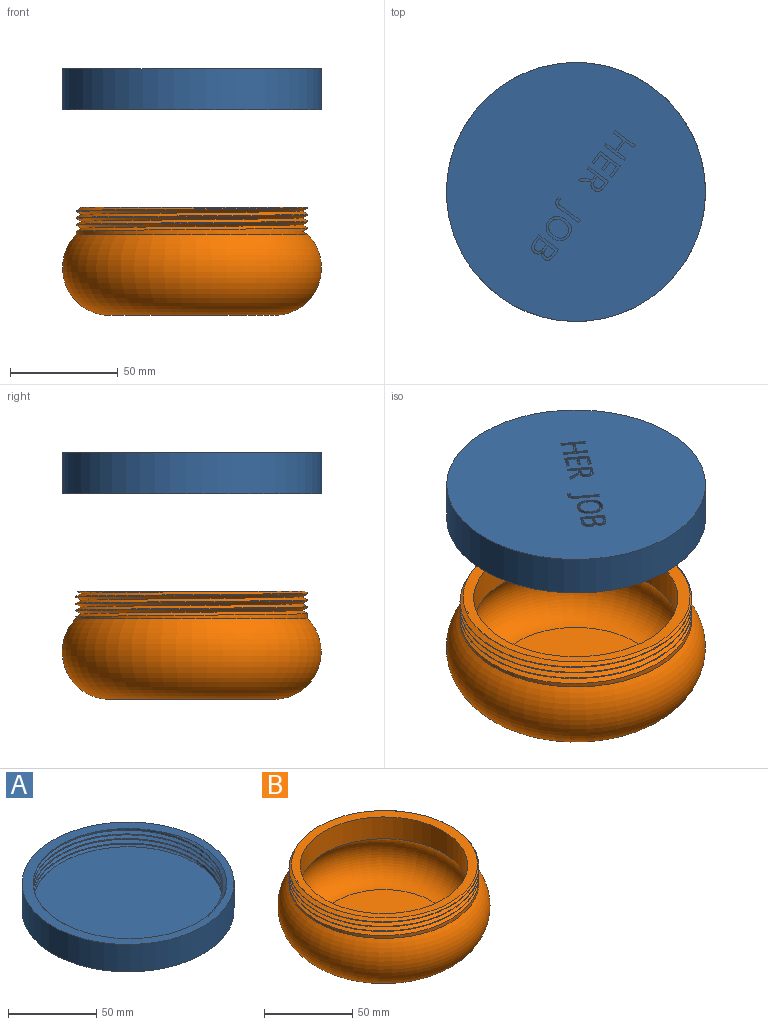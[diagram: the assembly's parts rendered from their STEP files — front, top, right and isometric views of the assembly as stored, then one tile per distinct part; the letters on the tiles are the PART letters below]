
ASSEMBLY  parts=2 mates=1
PART A: 118 faces, bbox 120.3x129.3x20.6 mm
  f0: plane 120.29x120.29mm, normal (0,0,-1), area 11030.5mm2, adj f1,f2,f3,f4,f5,f6,f7,f8
  f1: extruded ~4.33x2.54mm, area 11.8mm2, adj f0,f2,f8,f66
  f2: extruded ~3.87x2.54mm, area 11mm2, adj f0,f1,f3,f66
  f3: extruded ~3.91x2.54mm, area 11mm2, adj f0,f2,f4,f66
  f4: extruded ~4.37x2.54mm, area 11.9mm2, adj f0,f3,f5,f66
  f5: extruded ~4.34x2.54mm, area 11.8mm2, adj f0,f4,f6,f66
  f6: extruded ~3.92x2.54mm, area 11mm2, adj f0,f5,f7,f66
  f7: extruded ~3.86x2.54mm, area 10.9mm2, adj f0,f6,f8,f66
  f8: extruded ~4.33x2.54mm, area 11.8mm2, adj f0,f1,f7,f66
  f9: extruded ~2.54x1.16mm, area 3mm2, adj f0,f10,f18,f67
  f10: plane 2.54x1.14mm, normal (1,0,0), area 2.9mm2, adj f0,f9,f11,f67
  f11: extruded ~2.54x1.16mm, area 3mm2, adj f0,f10,f12,f67
  f12: extruded ~2.54x1.18mm, area 3.3mm2, adj f0,f11,f13,f67
  f13: extruded ~2.54x1.36mm, area 3.7mm2, adj f0,f12,f14,f67
  f14: plane 11.46x2.54mm, normal (1,0,0), area 29.1mm2, adj f0,f13,f15,f67
  f15: plane 2.54x1.33mm, normal (0,1,0), area 3.4mm2, adj f0,f14,f16,f67
  f16: plane 11.35x2.54mm, normal (-1,0,0), area 28.8mm2, adj f0,f15,f17,f67
  f17: extruded ~2.54x2.31mm, area 6.3mm2, adj f0,f16,f18,f67
  f18: extruded ~2.54x2.17mm, area 6.1mm2, adj f0,f9,f17,f67
  f19: plane 3.24x2.54mm, normal (0,1,0), area 8.2mm2, adj f0,f20,f29,f68
  f20: extruded ~3.3x2.54mm, area 8.7mm2, adj f0,f19,f21,f68
  f21: extruded ~2.54x2.16mm, area 6.3mm2, adj f0,f20,f22,f68
  f22: extruded ~2.54x1.68mm, area 4.6mm2, adj f0,f21,f23,f68
  f23: extruded ~2.54x1.66mm, area 4.8mm2, adj f0,f22,f24,f68
  f24: plane 2.54x0.08mm, normal (-1,0,0), area 0.2mm2, adj f0,f23,f25,f68
  f25: extruded ~2.74x2.61mm, area 10.7mm2, adj f0,f24,f26,f68
  f26: extruded ~2.54x2.4mm, area 6.9mm2, adj f0,f25,f27,f68
  f27: extruded ~2.91x2.54mm, area 7.9mm2, adj f0,f26,f28,f68
  f28: plane 4x2.54mm, normal (0,-1,0), area 10.2mm2, adj f0,f27,f29,f68
  f29: plane 11.46x2.54mm, normal (1,0,0), area 29.1mm2, adj f0,f19,f28,f68
  f30: cylinder r=60.14mm len=120.29mm, axis (0,0,-1), area 7198.8mm2, adj f0,f69
  f31: plane 6.39x2.54mm, normal (0,-1,0), area 16.2mm2, adj f0,f32,f42,f70
  f32: plane 11.46x2.54mm, normal (1,0,0), area 29.1mm2, adj f0,f31,f33,f70
  f33: plane 6.39x2.54mm, normal (0,1,0), area 16.2mm2, adj f0,f32,f34,f70
  f34: plane 2.54x1.18mm, normal (-1,0,0), area 3mm2, adj f0,f33,f35,f70
  f35: plane 5.06x2.54mm, normal (0,-1,0), area 12.8mm2, adj f0,f34,f36,f70
  f36: plane 3.69x2.54mm, normal (-1,0,0), area 9.4mm2, adj f0,f35,f37,f70
  f37: plane 4.75x2.54mm, normal (0,1,0), area 12.1mm2, adj f0,f36,f38,f70
  f38: plane 2.54x1.18mm, normal (-1,0,0), area 3mm2, adj f0,f37,f39,f70
  f39: plane 4.75x2.54mm, normal (0,-1,0), area 12.1mm2, adj f0,f38,f40,f70
  f40: plane 4.22x2.54mm, normal (-1,0,0), area 10.7mm2, adj f0,f39,f41,f70
  f41: plane 5.06x2.54mm, normal (0,1,0), area 12.8mm2, adj f0,f40,f42,f70
  f42: plane 2.54x1.19mm, normal (-1,0,0), area 3mm2, adj f0,f31,f41,f70
  f43: plane 4.77x2.54mm, normal (-1,0,0), area 12.1mm2, adj f0,f44,f53,f71
  f44: plane 2.54x1.33mm, normal (0,-1,0), area 3.4mm2, adj f0,f43,f45,f71
  f45: plane 11.46x2.54mm, normal (1,0,0), area 29.1mm2, adj f0,f44,f46,f71
  f46: plane 3.14x2.54mm, normal (0,1,0), area 8mm2, adj f0,f45,f47,f71
  f47: extruded ~3.12x2.54mm, area 8.3mm2, adj f0,f46,f48,f71
  f48: extruded ~2.54x2.43mm, area 6.9mm2, adj f0,f47,f49,f71
  f49: extruded ~3.07x2.54mm, area 10.5mm2, adj f0,f48,f50,f71
  f50: plane 5.15x3.11mm, normal (-0.86,0.52,0), area 15.3mm2, adj f0,f49,f51,f71
  f51: plane 2.54x1.58mm, normal (0,-1,0), area 4mm2, adj f0,f50,f52,f71
  f52: plane 4.77x2.77mm, normal (0.86,-0.5,0), area 14mm2, adj f0,f51,f53,f71
  f53: plane 2.54x2.39mm, normal (0,-1,0), area 6.1mm2, adj f0,f43,f52,f71
  f54: plane 2.54x1.33mm, normal (0,-1,0), area 3.4mm2, adj f0,f55,f65,f72
  f55: plane 5.39x2.54mm, normal (1,0,0), area 13.7mm2, adj f0,f54,f56,f72
  f56: plane 6.04x2.54mm, normal (0,-1,0), area 15.3mm2, adj f0,f55,f57,f72
  f57: plane 5.39x2.54mm, normal (-1,0,0), area 13.7mm2, adj f0,f56,f58,f72
  f58: plane 2.54x1.33mm, normal (0,-1,0), area 3.4mm2, adj f0,f57,f59,f72
  f59: plane 11.46x2.54mm, normal (1,0,0), area 29.1mm2, adj f0,f58,f60,f72
  f60: plane 2.54x1.33mm, normal (0,1,0), area 3.4mm2, adj f0,f59,f61,f72
  f61: plane 4.88x2.54mm, normal (-1,0,0), area 12.4mm2, adj f0,f60,f62,f72
  f62: plane 6.04x2.54mm, normal (0,1,0), area 15.3mm2, adj f0,f61,f63,f72
  f63: plane 4.88x2.54mm, normal (1,0,0), area 12.4mm2, adj f0,f62,f64,f72
  f64: plane 2.54x1.33mm, normal (0,1,0), area 3.4mm2, adj f0,f63,f65,f72
  f65: plane 11.46x2.54mm, normal (-1,0,0), area 29.1mm2, adj f0,f54,f64,f72
  f66: plane 11.8x10.54mm, normal (0,0,-1), area 41.6mm2, adj f1,f2,f3,f4,f5,f6,f7,f8
  f67: plane 14.48x4.08mm, normal (0,0,-1), area 21.4mm2, adj f9,f10,f11,f12,f13,f14,f15,f16
  f68: plane 11.46x7.94mm, normal (0,0,-1), area 44.8mm2, adj f19,f20,f21,f22,f23,f24,f25,f26
  f69: plane 120.29x120.29mm, normal (0,0,1), area 2042.1mm2, adj f30,f95,f96,f97,f98
  f70: plane 11.46x6.39mm, normal (0,0,-1), area 32.9mm2, adj f31,f32,f33,f34,f35,f36,f37,f38
  f71: plane 11.46x8.08mm, normal (0,0,-1), area 39.4mm2, adj f43,f44,f45,f46,f47,f48,f49,f50
  f72: plane 11.46x8.7mm, normal (0,0,-1), area 37.7mm2, adj f54,f55,f56,f57,f58,f59,f60,f61
  f73: extruded ~3.53x2.54mm, area 9.5mm2, adj f66,f74,f80,f106
  f74: extruded ~3.5x2.54mm, area 9.4mm2, adj f66,f73,f75,f106
  f75: extruded ~2.9x2.54mm, area 8.2mm2, adj f66,f74,f76,f106
  f76: extruded ~2.86x2.54mm, area 8.2mm2, adj f66,f75,f77,f106
  f77: extruded ~3.51x2.54mm, area 9.4mm2, adj f66,f76,f78,f106
  f78: extruded ~3.54x2.54mm, area 9.5mm2, adj f66,f77,f79,f106
  f79: extruded ~2.88x2.54mm, area 8.2mm2, adj f66,f78,f80,f106
  f80: extruded ~2.88x2.54mm, area 8.2mm2, adj f66,f73,f79,f106
  f81: plane 2.54x2.2mm, normal (0,1,0), area 5.6mm2, adj f68,f82,f87,f107
  f82: plane 3.75x2.54mm, normal (-1,0,0), area 9.5mm2, adj f68,f81,f83,f107
  f83: plane 2.54x1.96mm, normal (0,-1,0), area 5mm2, adj f68,f82,f84,f107
  f84: extruded ~2.54x2.2mm, area 5.7mm2, adj f68,f83,f85,f107
  f85: extruded ~2.54x1.39mm, area 4.1mm2, adj f68,f84,f86,f107
  f86: extruded ~2.54x1.49mm, area 4.3mm2, adj f68,f85,f87,f107
  f87: extruded ~2.54x2.03mm, area 5.4mm2, adj f68,f81,f86,f107
  f88: plane 4.29x2.54mm, normal (-1,0,0), area 10.9mm2, adj f68,f89,f94,f108
  f89: plane 2.54x2.28mm, normal (0,-1,0), area 5.8mm2, adj f68,f88,f90,f108
  f90: extruded ~2.54x2.18mm, area 5.8mm2, adj f68,f89,f91,f108
  f91: extruded ~2.54x1.57mm, area 4.6mm2, adj f68,f90,f92,f108
  f92: extruded ~2.54x1.68mm, area 4.8mm2, adj f68,f91,f93,f108
  f93: extruded ~2.54x2.09mm, area 5.6mm2, adj f68,f92,f94,f108
  f94: plane 2.54x2.39mm, normal (0,1,0), area 6.1mm2, adj f68,f88,f93,f108
  f95: cylinder r=53.79mm len=107.59mm, axis (0,0,-1), area 1027.7mm2, adj f69,f96,f97,f98,f109,f110,f111
  f96: revolved ~24.49x9.13mm, area 24.6mm2, adj f69,f95,f97
  f97: bspline ~129.3x112.15mm, area 3487.3mm2, adj f69,f95,f96,f98,f112,f113
  f98: bspline ~129.3x112.15mm, area 3246.5mm2, adj f69,f95,f97,f114
  f99: plane 2.54x1.83mm, normal (0,1,0), area 4.6mm2, adj f71,f100,f105,f115
  f100: plane 4.38x2.54mm, normal (-1,0,0), area 11.1mm2, adj f71,f99,f101,f115
  f101: plane 2.54x1.73mm, normal (0,-1,0), area 4.4mm2, adj f71,f100,f102,f115
  f102: extruded ~2.54x2.15mm, area 5.7mm2, adj f71,f101,f103,f115
  f103: extruded ~2.54x1.64mm, area 4.7mm2, adj f71,f102,f104,f115
  f104: extruded ~2.54x1.68mm, area 4.7mm2, adj f71,f103,f105,f115
  f105: extruded ~2.54x2.07mm, area 5.6mm2, adj f71,f99,f104,f115
  f106: plane 9.44x7.72mm, normal (0,0,-1), area 60.4mm2, adj f73,f74,f75,f76,f77,f78,f79,f80
  f107: plane 4.85x3.75mm, normal (0,0,-1), area 16.6mm2, adj f81,f82,f83,f84,f85,f86,f87
  f108: plane 5.18x4.29mm, normal (0,0,-1), area 20.3mm2, adj f88,f89,f90,f91,f92,f93,f94
  f109: plane 107.59x107.59mm, normal (0,0,1), area 9090.7mm2, adj f95,f112
  f110: revolved ~27.45x5.92mm, area 19mm2, adj f95,f111,f116,f117
  f111: revolved ~27.45x5.92mm, area 27.9mm2, adj f95,f110,f114,f116
  f112: cylinder r=53.79mm len=73.57mm, axis (0,0,1), area 52mm2, adj f97,f109,f117
  f113: revolved ~28.64x7.62mm, area 72.6mm2, adj f97,f114,f116,f117
  f114: revolved ~112.17x111.82mm, area 944.3mm2, adj f98,f111,f113,f116
  f115: plane 4.56x4.38mm, normal (0,0,-1), area 18mm2, adj f99,f100,f101,f102,f103,f104,f105
  f116: plane 2.54x2.31mm, normal (0.56,0.83,0), area 3.2mm2, adj f110,f111,f113,f114,f117
  f117: cylinder r=53.93mm len=27.41mm, axis (0,0,1), area 27.9mm2, adj f110,f112,f113,f116
PART B: 61 faces, bbox 130.9x130.9x52.6 mm
  f0: plane 76.2x76.2mm, normal (0,0,-1), area 4417.8mm2, adj f6,f15,f16,f17,f18,f19,f20,f21
  f1: cylinder r=53.79mm len=107.59mm, axis (0,0,-1), area 945.1mm2, adj f5,f6,f7,f8,f9,f10
  f2: plane 76.2x76.2mm, normal (0,0,1), area 4560.4mm2, adj f3
  f3: torus R=38.1mm, axis (0,0,-1), area 12404.7mm2, adj f2,f4
  f4: cylinder r=47.44mm len=94.89mm, axis (0,0,-1), area 4514.6mm2, adj f3,f5
  f5: plane 105.52x105.51mm, normal (0,0,1), area 1665.2mm2, adj f1,f4,f7,f8
  f6: torus R=38.1mm, axis (0,0,-1), area 17576.6mm2, adj f0,f1
  f7: bspline ~124.23x107.59mm, area 3493.8mm2, adj f1,f5,f8,f10
  f8: bspline ~124.23x107.59mm, area 3080.1mm2, adj f1,f5,f7,f9
  f9: plane 16.65x3.11mm, normal (0.5,0,-0.87), area 29.8mm2, adj f1,f8,f10
  f10: plane 16.65x3.11mm, normal (0.5,0,0.87), area 29.8mm2, adj f1,f7,f9
  f11: plane 3.55x2.54mm, normal (0.94,-0.35,0), area 9.6mm2, adj f12,f23,f24,f60
  f12: plane 3.71x2.54mm, normal (0,1,0), area 9.4mm2, adj f11,f13,f24,f60
  f13: plane 3.55x2.54mm, normal (-0.94,-0.35,0), area 9.6mm2, adj f12,f14,f24,f60
  f14: extruded ~2.54x1.65mm, area 4.4mm2, adj f13,f23,f24,f60
  f15: plane 3.65x2.54mm, normal (0.93,-0.36,0), area 9.9mm2, adj f0,f16,f22,f24
  f16: plane 2.54x1.38mm, normal (0,-1,0), area 3.5mm2, adj f0,f15,f17,f24
  f17: plane 11.51x4.51mm, normal (-0.93,0.36,0), area 31.4mm2, adj f0,f16,f18,f24
  f18: plane 2.54x1.12mm, normal (0,1,0), area 2.8mm2, adj f0,f17,f19,f24
  f19: plane 11.51x4.53mm, normal (0.93,0.37,0), area 31.4mm2, adj f0,f18,f20,f24
  f20: plane 2.54x1.35mm, normal (0,-1,0), area 3.4mm2, adj f0,f19,f21,f24
  f21: plane 3.65x2.54mm, normal (-0.93,-0.36,0), area 9.9mm2, adj f0,f20,f22,f24
  f22: plane 4.59x2.54mm, normal (0,-1,0), area 11.7mm2, adj f0,f15,f21,f24
  f23: extruded ~2.54x1.65mm, area 4.4mm2, adj f11,f14,f24,f60
  f24: plane 11.51x10.16mm, normal (0,0,-1), area 33.8mm2, adj f11,f12,f13,f14,f15,f16,f17,f18
  f25: plane 2.54x1.52mm, normal (0,-1,0), area 3.9mm2, adj f0,f26,f39,f40
  f26: plane 11.46x2.54mm, normal (-1,0,0), area 29.1mm2, adj f0,f25,f27,f40
  f27: plane 2.54x1.25mm, normal (0,1,0), area 3.2mm2, adj f0,f26,f28,f40
  f28: plane 6.58x2.54mm, normal (1,0,0), area 16.7mm2, adj f0,f27,f29,f40
  f29: extruded ~2.54x1.64mm, area 4.2mm2, adj f0,f28,f30,f40
  f30: extruded ~2.54x1.36mm, area 3.5mm2, adj f0,f29,f31,f40
  f31: plane 2.54x0.06mm, normal (0,1,0), area 0.2mm2, adj f0,f30,f32,f40
  f32: plane 9.58x6.25mm, normal (-0.84,0.55,0), area 29.1mm2, adj f0,f31,f33,f40
  f33: plane 2.54x1.51mm, normal (0,1,0), area 3.8mm2, adj f0,f32,f34,f40
  f34: plane 11.46x2.54mm, normal (1,0,0), area 29.1mm2, adj f0,f33,f35,f40
  f35: plane 2.54x1.23mm, normal (0,-1,0), area 3.1mm2, adj f0,f34,f36,f40
  f36: plane 6.51x2.54mm, normal (-1,0,0), area 16.5mm2, adj f0,f35,f37,f40
  f37: extruded ~3.1x2.54mm, area 7.9mm2, adj f0,f36,f38,f40
  f38: plane 2.54x0.06mm, normal (0,-1,0), area 0.2mm2, adj f0,f37,f39,f40
  f39: plane 9.62x6.26mm, normal (0.84,-0.55,0), area 29.2mm2, adj f0,f25,f38,f40
  f40: plane 11.46x8.95mm, normal (0,0,-1), area 43.4mm2, adj f25,f26,f27,f28,f29,f30,f31,f32
  f41: plane 10.16x3.89mm, normal (0.93,-0.36,0), area 27.6mm2, adj f0,f42,f58,f59
  f42: plane 2.54x1.07mm, normal (0,-1,0), area 2.7mm2, adj f0,f41,f43,f59
  f43: plane 10.14x3.92mm, normal (-0.93,-0.36,0), area 27.6mm2, adj f0,f42,f44,f59
  f44: plane 2.54x0.06mm, normal (0,-1,0), area 0.2mm2, adj f0,f43,f45,f59
  f45: extruded ~2.76x2.54mm, area 7mm2, adj f0,f44,f46,f59
  f46: plane 7.39x2.54mm, normal (1,0,0), area 18.8mm2, adj f0,f45,f47,f59
  f47: plane 2.54x1.33mm, normal (0,-1,0), area 3.4mm2, adj f0,f46,f48,f59
  f48: plane 11.46x2.54mm, normal (-1,0,0), area 29.1mm2, adj f0,f47,f49,f59
  f49: plane 2.54x1.99mm, normal (0,1,0), area 5.1mm2, adj f0,f48,f50,f59
  f50: plane 9.45x3.66mm, normal (0.93,0.36,0), area 25.8mm2, adj f0,f49,f51,f59
  f51: plane 2.54x0.06mm, normal (0,1,0), area 0.2mm2, adj f0,f50,f52,f59
  f52: plane 9.45x3.63mm, normal (-0.93,0.36,0), area 25.7mm2, adj f0,f51,f53,f59
  f53: plane 2.54x2.01mm, normal (0,1,0), area 5.1mm2, adj f0,f52,f54,f59
  f54: plane 11.46x2.54mm, normal (1,0,0), area 29.1mm2, adj f0,f53,f55,f59
  f55: plane 2.54x1.23mm, normal (0,-1,0), area 3.1mm2, adj f0,f54,f56,f59
  f56: plane 7.29x2.54mm, normal (-1,0,0), area 18.5mm2, adj f0,f55,f57,f59
  f57: extruded ~2.87x2.54mm, area 7.3mm2, adj f0,f56,f58,f59
  f58: plane 2.54x0.06mm, normal (0,-1,0), area 0.2mm2, adj f0,f41,f57,f59
  f59: plane 11.46x11.35mm, normal (0,0,-1), area 56.2mm2, adj f41,f42,f43,f44,f45,f46,f47,f48
  f60: plane 5.21x3.71mm, normal (0,0,-1), area 9.2mm2, adj f11,f12,f13,f14,f23
PLACE A rot(axis=(0.45,-0.89,0),180deg) t=(100.06,144.21,96.57)mm
PLACE B t=(-12.01,-1.74,-18.04)mm fixed
MATE cylindrical A.f0 <-> B.f1  axis (0,0,1) through (-12.01,-1.74,96.57)mm
